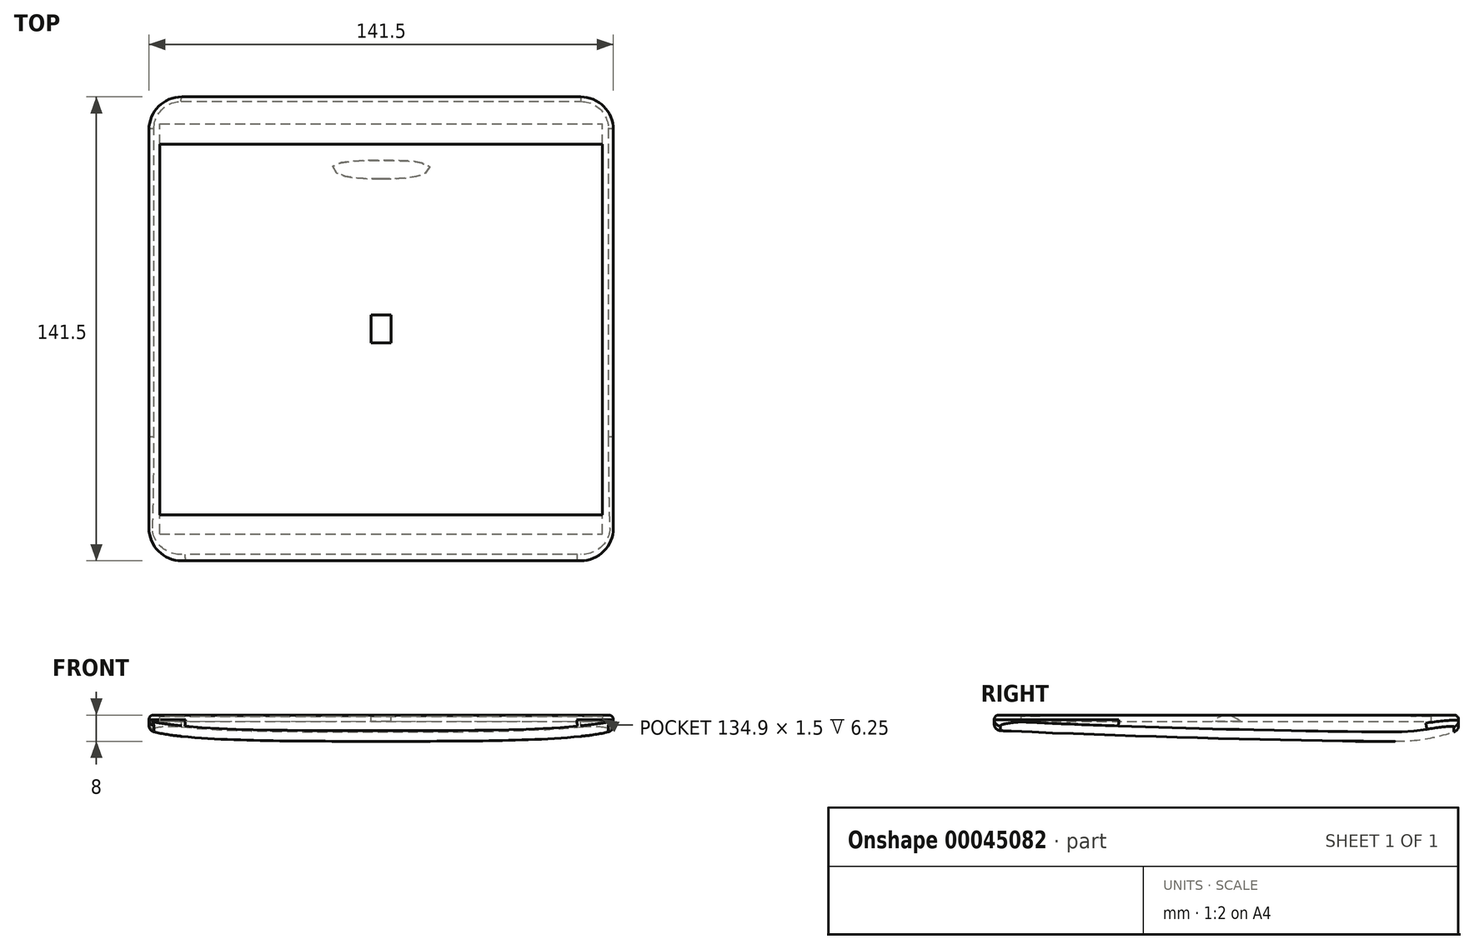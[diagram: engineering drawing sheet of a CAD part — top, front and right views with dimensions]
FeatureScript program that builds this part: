
annotation { "Feature Type Name" : "Feature", "Feature Type Description" : "" }
export const myFeature = defineFeature(function(context is Context, id is Id, definition is map)
    precondition{}
    {
        {
            var Q0;
            Q0=qCreatedBy(makeId("Top.planeOp"),FACE);
            var sketch = newSketch(context, id + "F0", { "sketchPlane" : qUnion([Q0])});
            skLineSegment(sketch, "E0.bottom", {"start": v(-60.75, 70.75) * mm, "end": v(60.75, 70.75) * mm});
            skLineSegment(sketch, "E0.top", {"start": v(-60.75, -70.75) * mm, "end": v(60.75, -70.75) * mm});
            skLineSegment(sketch, "E0.left", {"start": v(-70.75, 60.75) * mm, "end": v(-70.75, -60.75) * mm});
            skLineSegment(sketch, "E0.right", {"start": v(70.75, 60.75) * mm, "end": v(70.75, -60.75) * mm});
            skLineSegment(sketch, "E1", {"start": v(0, -18.4) * mm, "end": v(0, 26.9) * mm, "construction": true});
            skLineSegment(sketch, "E2", {"start": v(-17.11, 0) * mm, "end": v(20.4, 0) * mm, "construction": true});
            skLineSegment(sketch, "E3.bottom", {"start": v(-67.45, 56.25) * mm, "end": v(67.45, 56.25) * mm});
            skLineSegment(sketch, "E3.top", {"start": v(-67.45, -56.75) * mm, "end": v(67.45, -56.75) * mm});
            skLineSegment(sketch, "E3.left", {"start": v(-67.45, 56.25) * mm, "end": v(-67.45, -56.75) * mm});
            skLineSegment(sketch, "E3.right", {"start": v(67.45, 56.25) * mm, "end": v(67.45, -56.75) * mm});
            skPoint(sketch, "E4.visualSharp", {"position": v(-70.75, 70.75) * mm});
            skArc(sketch, "E4.filletArc", {"start": v(-60.75, 70.75) * mm, "mid": v(-67.82, 67.82) * mm, "end": v(-70.75, 60.75) * mm});
            skPoint(sketch, "E5.visualSharp", {"position": v(70.75, 70.75) * mm});
            skArc(sketch, "E5.filletArc", {"start": v(70.75, 60.75) * mm, "mid": v(67.82, 67.82) * mm, "end": v(60.75, 70.75) * mm});
            skPoint(sketch, "E6.visualSharp", {"position": v(70.75, -70.75) * mm});
            skArc(sketch, "E6.filletArc", {"start": v(60.75, -70.75) * mm, "mid": v(67.82, -67.82) * mm, "end": v(70.75, -60.75) * mm});
            skPoint(sketch, "E7.visualSharp", {"position": v(-70.75, -70.75) * mm});
            skArc(sketch, "E7.filletArc", {"start": v(-70.75, -60.75) * mm, "mid": v(-67.82, -67.82) * mm, "end": v(-60.75, -70.75) * mm});
            skSolve(sketch);
        }
        {
            var Q0;
            Q0=makeQuery(id+"F0.imprint","IMPRINT",FACE,{"disambiguationData":[TD([[makeQuery(id+"F0.imprint","IMPRINT",EDGE,{"derivedFrom":sQuery(id+"F0.wireOp",EDGE,"E0.bottom")}),-1.0]])]});
            var Q1;
            Q1=makeQuery(id+"F0.imprint","IMPRINT",FACE,{"disambiguationData":[TD([[makeQuery(id+"F0.imprint","IMPRINT",EDGE,{"derivedFrom":sQuery(id+"F0.wireOp",EDGE,"E3.bottom")}),-1.0]])]});
            extrude(context, id + "F1", {"entities" : qUnion([Q0, Q1]), "oppositeDirection" : true, "depth" : 8 * mm});
        }
        {
            var Q0;
            Q0=makeQuery(id+"F1.opExtrude","CAP_FACE",FACE,{"disambiguationData":[OSD([sQuery(id+"F0.wireOp",EDGE,"E0.bottom"),sQuery(id+"F0.wireOp",EDGE,"E0.top"),sQuery(id+"F0.wireOp",EDGE,"E0.left"),sQuery(id+"F0.wireOp",EDGE,"E0.right"),sQuery(id+"F0.wireOp",EDGE,"E4.filletArc"),sQuery(id+"F0.wireOp",EDGE,"E5.filletArc"),sQuery(id+"F0.wireOp",EDGE,"E6.filletArc"),sQuery(id+"F0.wireOp",EDGE,"E7.filletArc")])],"isStart":true});
            fillet(context, id + "F2", {"entities" : qUnion([Q0]), "radius" : 1.4 * mm, "tangentPropagation" : true, "allowEdgeOverflow" : false});
        }
        {
            var Q0;
            Q0=makeQuery(id+"F0.imprint","IMPRINT",FACE,{"disambiguationData":[TD([[makeQuery(id+"F0.imprint","IMPRINT",EDGE,{"derivedFrom":sQuery(id+"F0.wireOp",EDGE,"E3.bottom")}),-1.0]])]});
            var sketch = newSketch(context, id + "F3", { "sketchPlane" : qUnion([Q0])});
            skPoint(sketch, "E8.0", {"position": v(-69.35, 60.75) * mm});
            skLineSegment(sketch, "E9.0", {"start": v(60.75, 69.35) * mm, "end": v(-60.75, 69.35) * mm, "construction": true});
            skPoint(sketch, "E10.0", {"position": v(69.35, 60.75) * mm});
            skPoint(sketch, "E11.0", {"position": v(69.35, -60.75) * mm});
            skLineSegment(sketch, "E12.0", {"start": v(-60.75, -69.35) * mm, "end": v(60.75, -69.35) * mm, "construction": true});
            skPoint(sketch, "E13.0", {"position": v(-69.35, -60.75) * mm});
            skPoint(sketch, "E14", {"position": v(0, 69.35) * mm});
            skPoint(sketch, "E15", {"position": v(0, -69.35) * mm});
            skFitSpline(sketch, "E16", {"points": [v(0, 69.35) * mm, v(-10.2, 69.2) * mm, v(-16.16, 68.95) * mm, v(-19.64, 68.77) * mm, v(-22.7, 68.58) * mm, v(-25.45, 68.38) * mm, v(-28.97, 67.38) * mm, v(-31.2, 65.87) * mm, v(-32.53, 64.43) * mm, v(-33.04, 63.9) * mm, v(-69.35, 60.75) * mm], "startDerivative": vector(-63.22, -0.78) * mm, "endDerivative": vector(-16.46, -45.41) * mm});
            skFitSpline(sketch, "E17.MirrorCS", {"points": [v(0, 69.35) * mm, v(10.2, 69.2) * mm, v(16.16, 68.95) * mm, v(19.64, 68.77) * mm, v(22.7, 68.58) * mm, v(25.45, 68.38) * mm, v(28.97, 67.38) * mm, v(31.2, 65.87) * mm, v(32.53, 64.43) * mm, v(33.04, 63.9) * mm, v(69.35, 60.75) * mm], "startDerivative": vector(63.22, -0.78) * mm, "endDerivative": vector(16.46, -45.41) * mm});
            skFitSpline(sketch, "E18.MirrorCS", {"points": [v(0, 69.35) * mm, v(10.2, 69.2) * mm, v(16.16, 68.95) * mm, v(19.64, 68.77) * mm, v(22.7, 68.58) * mm, v(25.45, 68.38) * mm, v(28.97, 67.38) * mm, v(31.2, 65.87) * mm, v(32.53, 64.43) * mm, v(33.04, 63.9) * mm, v(69.35, 60.75) * mm], "startDerivative": vector(63.22, -0.78) * mm, "endDerivative": vector(16.46, -45.41) * mm});
            skFitSpline(sketch, "E19.MirrorCS", {"points": [v(0, 69.35) * mm, v(-10.2, 69.2) * mm, v(-16.16, 68.95) * mm, v(-19.64, 68.77) * mm, v(-22.7, 68.58) * mm, v(-25.45, 68.38) * mm, v(-28.97, 67.38) * mm, v(-31.2, 65.87) * mm, v(-32.53, 64.43) * mm, v(-33.04, 63.9) * mm, v(-69.35, 60.75) * mm], "startDerivative": vector(-63.22, -0.78) * mm, "endDerivative": vector(-16.46, -45.41) * mm});
            skFitSpline(sketch, "E20.MirrorCS", {"points": [v(0, -69.35) * mm, v(10.1, -69.35) * mm, v(16.15, -69.2) * mm, v(19.7, -69.04) * mm, v(22.77, -68.88) * mm, v(25.5, -68.7) * mm, v(29.1, -67.65) * mm, v(31.42, -66.02) * mm, v(32.67, -64.57) * mm, v(33.54, -62.91) * mm, v(34.08, -60.75) * mm], "startDerivative": vector(63.2, 0.78) * mm, "endDerivative": vector(9.15, 47.38) * mm});
            skFitSpline(sketch, "E21.MirrorCS", {"points": [v(0, -69.35) * mm, v(-10.1, -69.35) * mm, v(-16.15, -69.2) * mm, v(-19.7, -69.04) * mm, v(-22.77, -68.88) * mm, v(-25.5, -68.7) * mm, v(-29.1, -67.65) * mm, v(-31.42, -66.02) * mm, v(-32.67, -64.57) * mm, v(-33.54, -62.91) * mm, v(-34.08, -60.75) * mm], "startDerivative": vector(-63.2, 0.78) * mm, "endDerivative": vector(-9.15, 47.38) * mm});
            skLineSegment(sketch, "E22", {"start": v(-69.35, 60.75) * mm, "end": v(-69.35, -60.75) * mm});
            skLineSegment(sketch, "E23", {"start": v(69.35, -60.75) * mm, "end": v(69.35, 60.75) * mm});
            skSolve(sketch);
        }
        {
            var Q0;
            Q0=qCreatedBy(makeId("Top.planeOp"),FACE);
            var sketch = newSketch(context, id + "F4", { "sketchPlane" : qUnion([Q0])});
            skPoint(sketch, "E24.0", {"position": v(-67.45, -56.75) * mm});
            skPoint(sketch, "E25.0", {"position": v(67.45, 56.25) * mm});
            skLineSegment(sketch, "E26.bottom", {"start": v(-67.45, -56.75) * mm, "end": v(67.45, -56.75) * mm});
            skLineSegment(sketch, "E26.top", {"start": v(-67.45, 56.25) * mm, "end": v(67.45, 56.25) * mm});
            skLineSegment(sketch, "E26.left", {"start": v(-67.45, -56.75) * mm, "end": v(-67.45, 56.25) * mm});
            skLineSegment(sketch, "E26.right", {"start": v(67.45, -56.75) * mm, "end": v(67.45, 56.25) * mm});
            skSolve(sketch);
        }
        {
            var Q0;
            Q0 = qSketchRegion(id + "F4", true);
            extrude(context, id + "F5", {"entities" : qUnion([Q0]), "operationType" : NewBodyOperationType.REMOVE, "oppositeDirection" : true, "depth" : 2 * mm});
        }
        {
            var Q0;
            Q0=qCreatedBy(makeId("Right.planeOp"),FACE);
            var sketch = newSketch(context, id + "F6", { "sketchPlane" : qUnion([Q0])});
            skFitSpline(sketch, "E27", {"points": [v(70.75, -4.7) * mm, v(45.75, -8) * mm, v(-70.75, -4.7) * mm], "startDerivative": vector(-94.5, -31.18) * mm, "endDerivative": vector(-224.21, 10.1) * mm});
            skLineSegment(sketch, "E28.0", {"start": v(70.75, -8) * mm, "end": v(70.75, -1.4) * mm});
            skLineSegment(sketch, "E29.0", {"start": v(-70.75, -8) * mm, "end": v(-70.75, -1.4) * mm, "construction": true});
            skLineSegment(sketch, "E30.0", {"start": v(60.75, -8) * mm, "end": v(-60.75, -8) * mm});
            skSolve(sketch);
        }
        {
            var Q0;
            Q0=makeQuery(id+"F1.opExtrude","SWEPT_FACE",FACE,{"disambiguationData":[OSD([sQuery(id+"F0.wireOp",EDGE,"E0.bottom")])]});
            cPlane(context, id + "F7", {"entities" : qUnion([Q0]), "cplaneType" : CPlaneType.OFFSET, "offset" : 0 * mm, "oppositeDirection" : true, "width" : 150 * mm, "height" : 150 * mm});
        }
        {
            var Q0;
            Q0=qCreatedBy(id+"F7.planeOp",FACE);
            var sketch = newSketch(context, id + "F8", { "sketchPlane" : qUnion([Q0])});
            skLineSegment(sketch, "E31.0", {"start": v(-70.75, -8) * mm, "end": v(-70.75, -1.4) * mm, "construction": true});
            skLineSegment(sketch, "E32.0", {"start": v(70.75, -8) * mm, "end": v(70.75, -1.4) * mm, "construction": true});
            skPoint(sketch, "E33.0", {"position": v(0, -8) * mm});
            skLineSegment(sketch, "E34", {"start": v(70.75, -13.32) * mm, "end": v(-70.75, -13.32) * mm});
            skPoint(sketch, "E35.0", {"position": v(0, -4.7) * mm});
            skFitSpline(sketch, "E36", {"points": [v(-70.75, -1.4) * mm, v(0, -4.7) * mm, v(70.75, -1.4) * mm], "startDerivative": vector(60, -19.8) * mm, "endDerivative": vector(60, 19.8) * mm});
            skLineSegment(sketch, "E37.0", {"start": v(-60.75, -8) * mm, "end": v(-60.75, -1.4) * mm});
            skLineSegment(sketch, "E37.1", {"start": v(60.75, -8) * mm, "end": v(60.75, -1.4) * mm});
            skLineSegment(sketch, "E38", {"start": v(-70.75, -1.4) * mm, "end": v(-70.75, -13.32) * mm});
            skLineSegment(sketch, "E39", {"start": v(70.75, -13.32) * mm, "end": v(70.75, -1.4) * mm});
            skSolve(sketch);
        }
        {
            var Q0;
            Q0=makeQuery(id+"F8.imprint","IMPRINT",FACE,{"disambiguationData":[TD([[makeQuery(id+"F8.imprint","IMPRINT",EDGE,{"derivedFrom":sQuery(id+"F8.wireOp",EDGE,"E34")}),-1.0]])]});
            var Q1;
            Q1=sQuery(id+"F6.wireOp",EDGE,"E27");
            sweep(context, id + "F9", {"operationType" : NewBodyOperationType.REMOVE, "profiles" : qUnion([Q0]), "path" : qUnion([Q1]), "keepProfileOrientation" : true});
        }
        {
            var Q0;
            Q0=makeQuery(id+"F9.boolean.opBoolean","COPY",FACE,{"derivedFrom":makeQuery(id+"F9.opSweep","SWEPT_FACE",FACE,{"disambiguationData":[OSD([sQuery(id+"F6.wireOp",EDGE,"E27"),sQuery(id+"F8.wireOp",EDGE,"E36")])]})});
            fillet(context, id + "F10", {"entities" : qUnion([Q0]), "radius" : 2 * mm, "tangentPropagation" : true, "allowEdgeOverflow" : false});
        }
        {
            var Q0;
            Q0=qCreatedBy(makeId("Front.planeOp"),FACE);
            var sketch = newSketch(context, id + "F11", { "sketchPlane" : qUnion([Q0])});
            skLineSegment(sketch, "E40.0", {"start": v(-67.45, -2) * mm, "end": v(67.45, -2) * mm});
            skLineSegment(sketch, "E41", {"start": v(-67.45, -2) * mm, "end": v(-67.45, -0.5) * mm});
            skLineSegment(sketch, "E42", {"start": v(-67.45, -0.5) * mm, "end": v(67.45, -0.5) * mm});
            skLineSegment(sketch, "E43", {"start": v(67.45, -0.5) * mm, "end": v(67.45, -2) * mm});
            skSolve(sketch);
        }
        {
            var Q0;
            Q0=makeQuery(id+"F11.imprint","IMPRINT",FACE,{"disambiguationData":[TD([[makeQuery(id+"F11.imprint","IMPRINT",EDGE,{"derivedFrom":sQuery(id+"F11.wireOp",EDGE,"E40.0")}),1.0]])]});
            extrude(context, id + "F12", {"entities" : qUnion([Q0]), "operationType" : NewBodyOperationType.REMOVE, "endBound" : BoundingType.SYMMETRIC, "oppositeDirection" : true, "depth" : 125 * mm});
        }
        {
            var Q0;
            Q0=qCreatedBy(makeId("Right.planeOp"),FACE);
            var sketch = newSketch(context, id + "F13", { "sketchPlane" : qUnion([Q0])});
            skLineSegment(sketch, "E44.0.0", {"start": v(-56.75, -0.1) * mm, "end": v(56.25, -0.1) * mm, "construction": true});
            skLineSegment(sketch, "E44.0.1", {"start": v(56.25, -0.1) * mm, "end": v(56.25, -0.5) * mm, "construction": true});
            skLineSegment(sketch, "E44.0.2", {"start": v(-56.75, -0.5) * mm, "end": v(56.25, -0.5) * mm, "construction": true});
            skFitSpline(sketch, "E44.0.3", {"points": [v(67.73, -0.5) * mm, v(67.87, -0.62) * mm, v(67.97, -0.75) * mm, v(68.05, -0.9) * mm, v(68.13, -1.06) * mm, v(68.17, -1.23) * mm, v(68.17, -1.4) * mm], "construction": true});
            skLineSegment(sketch, "E44.0.4", {"start": v(-56.3, -1.4) * mm, "end": v(68.17, -1.78) * mm, "construction": true});
            skFitSpline(sketch, "E44.0.5", {"points": [v(68.17, -1.78) * mm, v(68.17, -1.85) * mm, v(68.17, -1.93) * mm, v(68.16, -2) * mm], "construction": true});
            skLineSegment(sketch, "E44.0.6", {"start": v(68.16, -2) * mm, "end": v(-56.75, -2) * mm, "construction": true});
            skLineSegment(sketch, "E44.0.7", {"start": v(-56.75, -2) * mm, "end": v(-56.75, -0.1) * mm, "construction": true});
            skArc(sketch, "E45", {"start": v(4.24, -2) * mm, "mid": v(0, -0.25) * mm, "end": v(-4.24, -2) * mm});
            skLineSegment(sketch, "E46", {"start": v(4.24, -2) * mm, "end": v(-4.24, -2) * mm});
            skSolve(sketch);
        }
        {
            var Q0;
            Q0=makeQuery(id+"F13.imprint","IMPRINT",FACE,{"disambiguationData":[TD([[makeQuery(id+"F13.imprint","IMPRINT",EDGE,{"derivedFrom":sQuery(id+"F13.wireOp",EDGE,"E45")}),1.0]])]});
            extrude(context, id + "F14", {"entities" : qUnion([Q0]), "operationType" : NewBodyOperationType.ADD, "endBound" : BoundingType.SYMMETRIC, "depth" : 6 * mm});
        }
    });
